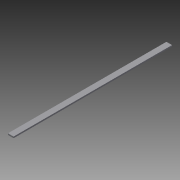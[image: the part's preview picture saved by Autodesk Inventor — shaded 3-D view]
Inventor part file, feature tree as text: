
AUTODESK INVENTOR PART (.ipt)
format: ipt  version: 2015 (Build 190159000, 159)  size: 74,240 bytes
history: native  units: in
note: dims shown in document units (in); Inventor stores cm internally (conversion verified against a paired STEP export)
features: extrude x2, sketch x2
ambient origin geometry x8: Origin, YZ Plane, XZ Plane, XY Plane, X Axis, Y Axis, Z Axis, Center Point
bodies: Solid1 (feature_tree)
feature tree (4):
  extrude  "Extrusion1"  Depth=0.125in
  extrude  "Extrusion2"  Depth=14.0in TaperAngle=0.0deg
  sketch  "Sketch1"  dims[d0=1.5in d1=0.125in]
  sketch  "Sketch2"  dims[d2=14.0in d3=0.0in d4=1.0in d5=0.0in]
